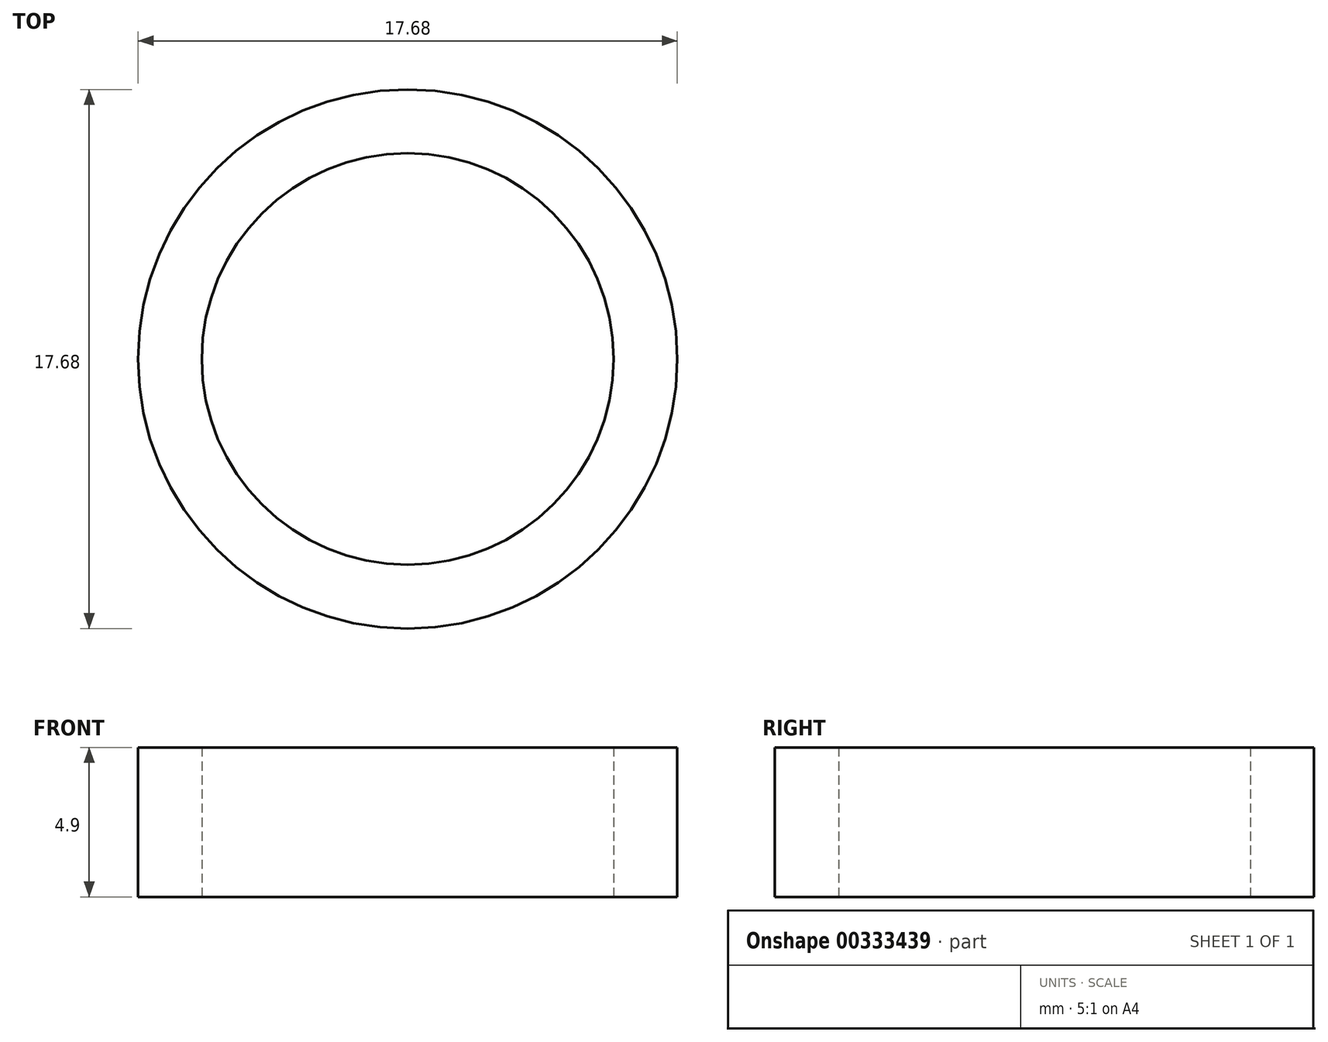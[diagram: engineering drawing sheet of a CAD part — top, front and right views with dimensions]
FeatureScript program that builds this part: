
annotation { "Feature Type Name" : "Feature", "Feature Type Description" : "" }
export const myFeature = defineFeature(function(context is Context, id is Id, definition is map)
    precondition{}
    {
        {
            var Q0;
            Q0=qCreatedBy(makeId("Top.planeOp"),FACE);
            var sketch = newSketch(context, id + "F0", { "sketchPlane" : qUnion([Q0])});
            skCircle(sketch, "E0", {"center": v(0, 0) * mm, "radius": 6.75 * mm});
            skCircle(sketch, "E1", {"center": v(0, 0) * mm, "radius": 8.84 * mm});
            skSolve(sketch);
        }
        {
            var Q0;
            Q0=makeQuery(id+"F0.imprint","IMPRINT",FACE,{"disambiguationData":[TD([[makeQuery(id+"F0.imprint","IMPRINT",EDGE,{"derivedFrom":sQuery(id+"F0.wireOp",EDGE,"E0")}),-1.0]])]});
            extrude(context, id + "F1", {"entities" : qUnion([Q0]), "depth" : 4.9 * mm});
        }
    });
